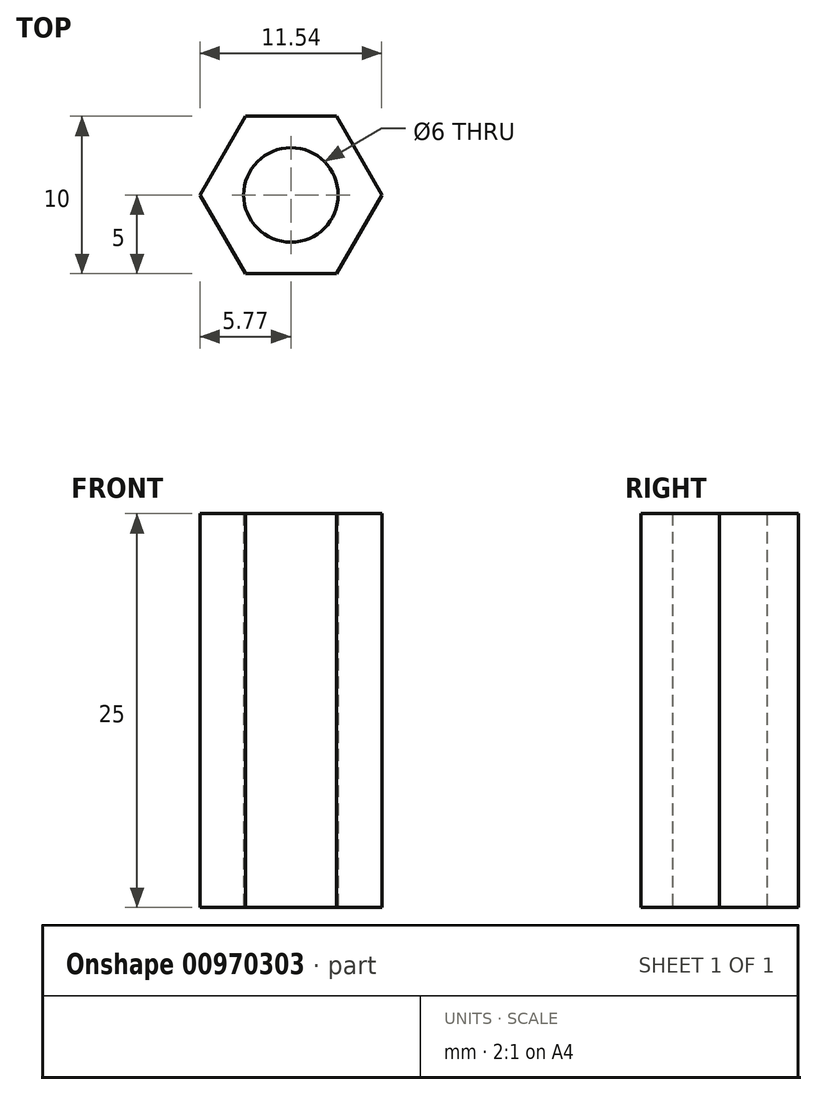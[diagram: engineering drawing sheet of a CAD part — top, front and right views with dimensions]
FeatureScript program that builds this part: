
annotation { "Feature Type Name" : "Feature", "Feature Type Description" : "" }
export const myFeature = defineFeature(function(context is Context, id is Id, definition is map)
    precondition{}
    {
        {
            var Q0;
            Q0=qCreatedBy(makeId("Top.planeOp"),FACE);
            var sketch = newSketch(context, id + "F0", { "sketchPlane" : qUnion([Q0])});
            skCircle(sketch, "E0.cCircle", {"center": v(0, 0) * mm, "radius": 5 * mm, "construction": true});
            skLineSegment(sketch, "E0.0", {"start": v(-2.89, 5) * mm, "end": v(2.89, 5) * mm});
            skLineSegment(sketch, "E0.1", {"start": v(2.89, 5) * mm, "end": v(5.77, 0) * mm});
            skLineSegment(sketch, "E0.2", {"start": v(5.77, 0) * mm, "end": v(2.89, -5) * mm});
            skLineSegment(sketch, "E0.3", {"start": v(2.89, -5) * mm, "end": v(-2.89, -5) * mm});
            skLineSegment(sketch, "E0.4", {"start": v(-2.89, -5) * mm, "end": v(-5.77, 0) * mm});
            skLineSegment(sketch, "E0.5", {"start": v(-5.77, 0) * mm, "end": v(-2.89, 5) * mm});
            skPoint(sketch, "E0.0.midPoint", {"position": v(0, 5) * mm});
            skCircle(sketch, "E1", {"center": v(0, 0) * mm, "radius": 3 * mm});
            skSolve(sketch);
        }
        {
            var Q0;
            Q0 = qSketchRegion(id + "F0", true);
            extrude(context, id + "F1", {"entities" : qUnion([Q0]), "depth" : 25 * mm, "offsetDistance" : 25 * mm});
        }
    });
